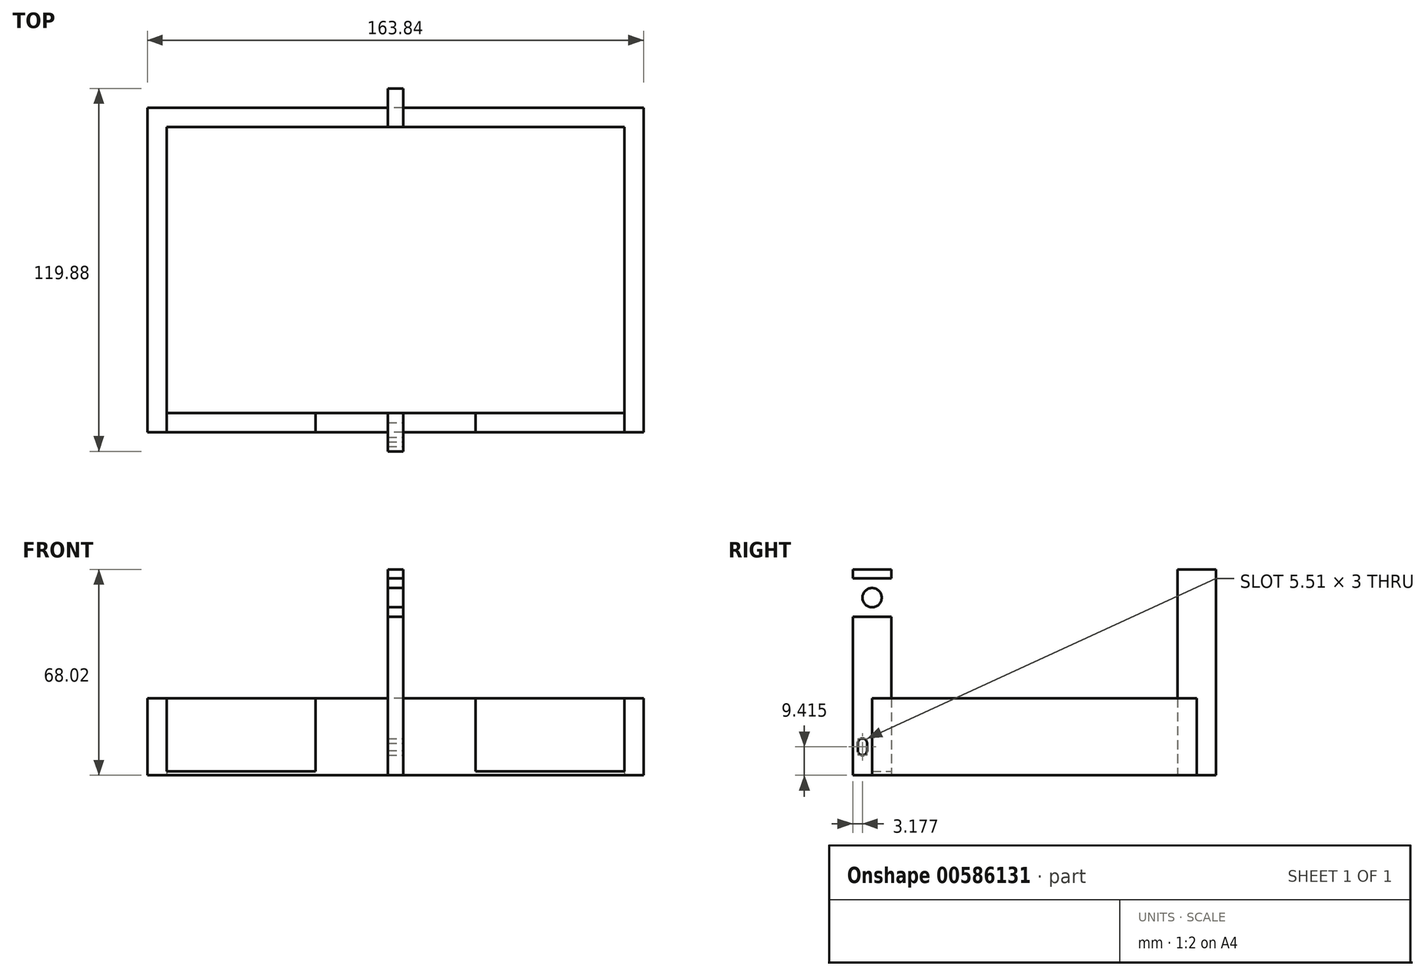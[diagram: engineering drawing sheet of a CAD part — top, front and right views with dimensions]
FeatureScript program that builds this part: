
annotation { "Feature Type Name" : "Feature", "Feature Type Description" : "" }
export const myFeature = defineFeature(function(context is Context, id is Id, definition is map)
    precondition{}
    {
        {
            var Q0;
            Q0=qCreatedBy(makeId("Top.planeOp"),FACE);
            var sketch = newSketch(context, id + "F0", { "sketchPlane" : qUnion([Q0])});
            skLineSegment(sketch, "E0.bottom", {"start": v(75.57, 47.24) * mm, "end": v(-75.57, 47.24) * mm});
            skLineSegment(sketch, "E0.top", {"start": v(75.57, -47.24) * mm, "end": v(-75.57, -47.24) * mm});
            skLineSegment(sketch, "E0.left", {"start": v(75.57, 47.24) * mm, "end": v(75.57, -47.24) * mm});
            skLineSegment(sketch, "E0.right", {"start": v(-75.57, 47.24) * mm, "end": v(-75.57, -47.24) * mm});
            skPoint(sketch, "E0.middle", {"position": v(0, 0) * mm});
            skLineSegment(sketch, "E1.bottom", {"start": v(81.92, 53.6) * mm, "end": v(-81.92, 53.6) * mm});
            skLineSegment(sketch, "E1.top", {"start": v(81.92, -53.6) * mm, "end": v(-81.92, -53.6) * mm});
            skLineSegment(sketch, "E1.left", {"start": v(81.92, 53.6) * mm, "end": v(81.92, -53.6) * mm});
            skLineSegment(sketch, "E1.right", {"start": v(-81.92, 53.6) * mm, "end": v(-81.92, -53.6) * mm});
            skLineSegment(sketch, "E2.bottom", {"start": v(-2.54, 47.24) * mm, "end": v(2.54, 47.24) * mm});
            skLineSegment(sketch, "E2.top", {"start": v(-2.54, 59.94) * mm, "end": v(2.54, 59.94) * mm});
            skLineSegment(sketch, "E2.left", {"start": v(-2.54, 47.24) * mm, "end": v(-2.54, 59.94) * mm});
            skLineSegment(sketch, "E2.right", {"start": v(2.54, 47.24) * mm, "end": v(2.54, 59.94) * mm});
            skPoint(sketch, "E2.middle", {"position": v(0, 53.6) * mm});
            skLineSegment(sketch, "E3.bottom", {"start": v(-2.54, -47.24) * mm, "end": v(2.54, -47.24) * mm});
            skLineSegment(sketch, "E3.top", {"start": v(-2.54, -59.94) * mm, "end": v(2.54, -59.94) * mm});
            skLineSegment(sketch, "E3.left", {"start": v(-2.54, -47.24) * mm, "end": v(-2.54, -59.94) * mm});
            skLineSegment(sketch, "E3.right", {"start": v(2.54, -47.24) * mm, "end": v(2.54, -59.94) * mm});
            skPoint(sketch, "E3.middle", {"position": v(0, -53.6) * mm});
            skLineSegment(sketch, "E4", {"start": v(-75.57, -47.24) * mm, "end": v(-75.57, -53.6) * mm});
            skLineSegment(sketch, "E5", {"start": v(75.57, -47.24) * mm, "end": v(75.57, -53.6) * mm});
            skLineSegment(sketch, "E6", {"start": v(-26.4, -47.24) * mm, "end": v(-26.4, -53.6) * mm});
            skLineSegment(sketch, "E7.MirrorCS", {"start": v(26.4, -47.24) * mm, "end": v(26.4, -53.6) * mm});
            skSolve(sketch);
        }
        {
            var Q0;
            {var subQ0=sQuery(id+"F0.wireOp",EDGE,"E4");Q0=makeQuery(id+"F0.imprint","IMPRINT",FACE,{"disambiguationData":[TD([[makeQuery(id+"F0.imprint","IMPRINT",EDGE,{"derivedFrom":subQ0}),1.0]])]});}
            var Q1;
            {var subQ6=sQuery(id+"F0.wireOp",EDGE,"E0.right");Q1=makeQuery(id+"F0.imprint","IMPRINT",FACE,{"disambiguationData":[TD([[makeQuery(id+"F0.imprint","IMPRINT",EDGE,{"derivedFrom":subQ6}),-1.0]])]});}
            var Q2;
            {var subQ5=sQuery(id+"F0.wireOp",EDGE,"E2.top");Q2=makeQuery(id+"F0.imprint","IMPRINT",FACE,{"disambiguationData":[TD([[makeQuery(id+"F0.imprint","IMPRINT",EDGE,{"derivedFrom":subQ5}),-1.0]])]});}
            var Q3;
            {var subQ5=sQuery(id+"F0.wireOp",EDGE,"E2.bottom");Q3=makeQuery(id+"F0.imprint","IMPRINT",FACE,{"disambiguationData":[TD([[makeQuery(id+"F0.imprint","IMPRINT",EDGE,{"derivedFrom":subQ5}),1.0]])]});}
            var Q4;
            {var subQ6=sQuery(id+"F0.wireOp",EDGE,"E0.left");Q4=makeQuery(id+"F0.imprint","IMPRINT",FACE,{"disambiguationData":[TD([[makeQuery(id+"F0.imprint","IMPRINT",EDGE,{"derivedFrom":subQ6}),1.0]])]});}
            var Q5;
            {var subQ0=sQuery(id+"F0.wireOp",EDGE,"E5");Q5=makeQuery(id+"F0.imprint","IMPRINT",FACE,{"disambiguationData":[TD([[makeQuery(id+"F0.imprint","IMPRINT",EDGE,{"derivedFrom":subQ0}),-1.0]])]});}
            var Q6;
            {var subQ3=sQuery(id+"F0.wireOp",EDGE,"E6");Q6=makeQuery(id+"F0.imprint","IMPRINT",FACE,{"disambiguationData":[TD([[makeQuery(id+"F0.imprint","IMPRINT",EDGE,{"derivedFrom":subQ3}),1.0]])]});}
            var Q7;
            {var subQ5=sQuery(id+"F0.wireOp",EDGE,"E3.bottom");Q7=makeQuery(id+"F0.imprint","IMPRINT",FACE,{"disambiguationData":[TD([[makeQuery(id+"F0.imprint","IMPRINT",EDGE,{"derivedFrom":subQ5}),-1.0]])]});}
            var Q8;
            {var subQ3=sQuery(id+"F0.wireOp",EDGE,"E7.MirrorCS");Q8=makeQuery(id+"F0.imprint","IMPRINT",FACE,{"disambiguationData":[TD([[makeQuery(id+"F0.imprint","IMPRINT",EDGE,{"derivedFrom":subQ3}),-1.0]])]});}
            var Q9;
            {var subQ5=sQuery(id+"F0.wireOp",EDGE,"E3.top");Q9=makeQuery(id+"F0.imprint","IMPRINT",FACE,{"disambiguationData":[TD([[makeQuery(id+"F0.imprint","IMPRINT",EDGE,{"derivedFrom":subQ5}),1.0]])]});}
            extrude(context, id + "F1", {"entities" : qUnion([Q0, Q1, Q2, Q3, Q4, Q5, Q6, Q7, Q8, Q9]), "depth" : 1.27 * mm, "offsetDistance" : 25.4 * mm});
        }
        {
            var Q0;
            {var subQ6=sQuery(id+"F0.wireOp",EDGE,"E0.right");Q0=makeQuery(id+"F0.imprint","IMPRINT",FACE,{"disambiguationData":[TD([[makeQuery(id+"F0.imprint","IMPRINT",EDGE,{"derivedFrom":subQ6}),-1.0]])]});}
            var Q1;
            {var subQ5=sQuery(id+"F0.wireOp",EDGE,"E2.top");Q1=makeQuery(id+"F0.imprint","IMPRINT",FACE,{"disambiguationData":[TD([[makeQuery(id+"F0.imprint","IMPRINT",EDGE,{"derivedFrom":subQ5}),-1.0]])]});}
            var Q2;
            {var subQ5=sQuery(id+"F0.wireOp",EDGE,"E2.bottom");Q2=makeQuery(id+"F0.imprint","IMPRINT",FACE,{"disambiguationData":[TD([[makeQuery(id+"F0.imprint","IMPRINT",EDGE,{"derivedFrom":subQ5}),1.0]])]});}
            var Q3;
            {var subQ6=sQuery(id+"F0.wireOp",EDGE,"E0.left");Q3=makeQuery(id+"F0.imprint","IMPRINT",FACE,{"disambiguationData":[TD([[makeQuery(id+"F0.imprint","IMPRINT",EDGE,{"derivedFrom":subQ6}),1.0]])]});}
            var Q4;
            {var subQ3=sQuery(id+"F0.wireOp",EDGE,"E7.MirrorCS");Q4=makeQuery(id+"F0.imprint","IMPRINT",FACE,{"disambiguationData":[TD([[makeQuery(id+"F0.imprint","IMPRINT",EDGE,{"derivedFrom":subQ3}),-1.0]])]});}
            var Q5;
            {var subQ5=sQuery(id+"F0.wireOp",EDGE,"E3.bottom");Q5=makeQuery(id+"F0.imprint","IMPRINT",FACE,{"disambiguationData":[TD([[makeQuery(id+"F0.imprint","IMPRINT",EDGE,{"derivedFrom":subQ5}),-1.0]])]});}
            var Q6;
            {var subQ3=sQuery(id+"F0.wireOp",EDGE,"E6");Q6=makeQuery(id+"F0.imprint","IMPRINT",FACE,{"disambiguationData":[TD([[makeQuery(id+"F0.imprint","IMPRINT",EDGE,{"derivedFrom":subQ3}),1.0]])]});}
            var Q7;
            {var subQ5=sQuery(id+"F0.wireOp",EDGE,"E3.top");Q7=makeQuery(id+"F0.imprint","IMPRINT",FACE,{"disambiguationData":[TD([[makeQuery(id+"F0.imprint","IMPRINT",EDGE,{"derivedFrom":subQ5}),1.0]])]});}
            extrude(context, id + "F2", {"entities" : qUnion([Q0, Q1, Q2, Q3, Q4, Q5, Q6, Q7]), "operationType" : NewBodyOperationType.ADD, "depth" : 25.4 * mm, "offsetDistance" : 25.4 * mm});
        }
        {
            var Q0;
            Q0=makeQuery(id+"F2.opExtrude","CAP_FACE",FACE,{"disambiguationData":[OSD([sQuery(id+"F0.wireOp",EDGE,"E0.bottom"),sQuery(id+"F0.wireOp",EDGE,"E0.left"),sQuery(id+"F0.wireOp",EDGE,"E0.right"),sQuery(id+"F0.wireOp",EDGE,"E1.bottom"),sQuery(id+"F0.wireOp",EDGE,"E1.top"),sQuery(id+"F0.wireOp",EDGE,"E1.left"),sQuery(id+"F0.wireOp",EDGE,"E1.right"),sQuery(id+"F0.wireOp",EDGE,"E2.bottom"),sQuery(id+"F0.wireOp",EDGE,"E2.top"),sQuery(id+"F0.wireOp",EDGE,"E2.left"),sQuery(id+"F0.wireOp",EDGE,"E2.right"),sQuery(id+"F0.wireOp",EDGE,"E4"),sQuery(id+"F0.wireOp",EDGE,"E5")])],"isStart":false});
            var sketch = newSketch(context, id + "F3", { "sketchPlane" : qUnion([Q0])});
            skLineSegment(sketch, "E8.bottom", {"start": v(-2.54, 59.94) * mm, "end": v(2.54, 59.94) * mm});
            skLineSegment(sketch, "E8.top", {"start": v(-2.54, 47.24) * mm, "end": v(2.54, 47.24) * mm});
            skLineSegment(sketch, "E8.left", {"start": v(-2.54, 59.94) * mm, "end": v(-2.54, 47.24) * mm});
            skLineSegment(sketch, "E8.right", {"start": v(2.54, 59.94) * mm, "end": v(2.54, 47.24) * mm});
            skLineSegment(sketch, "E9.MirrorCS", {"start": v(-2.54, -47.24) * mm, "end": v(2.54, -47.24) * mm});
            skLineSegment(sketch, "E10.MirrorCS", {"start": v(2.54, -59.94) * mm, "end": v(2.54, -47.24) * mm});
            skLineSegment(sketch, "E11.MirrorCS", {"start": v(-2.54, -59.94) * mm, "end": v(2.54, -59.94) * mm});
            skLineSegment(sketch, "E12.MirrorCS", {"start": v(-2.54, -59.94) * mm, "end": v(-2.54, -47.24) * mm});
            skSolve(sketch);
        }
        {
            var Q0;
            {var subQ5=sQuery(id+"F3.wireOp",EDGE,"E8.bottom");Q0=makeQuery(id+"F3.imprint","IMPRINT",FACE,{"disambiguationData":[TD([[makeQuery(id+"F3.imprint","IMPRINT",EDGE,{"derivedFrom":subQ5}),-1.0]])]});}
            var Q1;
            Q1=makeQuery(id+"F3.imprint","IMPRINT",FACE,{"disambiguationData":[TD([[makeQuery(id+"F3.imprint","IMPRINT",EDGE,{"derivedFrom":sQuery(id+"F3.wireOp",EDGE,"E9.MirrorCS")}),-1.0]])]});
            extrude(context, id + "F4", {"entities" : qUnion([Q0, Q1]), "operationType" : NewBodyOperationType.ADD, "depth" : 39.62 * mm + 3 * mm, "offsetDistance" : 25.4 * mm});
        }
        {
            var Q0;
            {var subQ0=sQuery(id+"F0.wireOp",EDGE,"E3.right");Q0=makeQuery(id+"F4.boolean.opBoolean","MERGE",FACE,{"derivedFrom":[makeQuery(id+"F2.boolean.opBoolean","MERGE",FACE,{"derivedFrom":[makeQuery(id+"F1.opExtrude","SWEPT_FACE",FACE,{"disambiguationData":[OSD([subQ0])]}),makeQuery(id+"F2.opExtrude","SWEPT_FACE",FACE,{"disambiguationData":[OSD([subQ0])]})]}),makeQuery(id+"F4.opExtrude","SWEPT_FACE",FACE,{"disambiguationData":[OSD([sQuery(id+"F3.wireOp",EDGE,"E10.MirrorCS")])]})]});}
            var sketch = newSketch(context, id + "F5", { "sketchPlane" : qUnion([Q0])});
            skCircle(sketch, "E13", {"center": v(-56.76, 8.16) * mm, "radius": 1.5 * mm});
            skCircle(sketch, "E14", {"center": v(-56.76, 10.67) * mm, "radius": 1.5 * mm});
            skLineSegment(sketch, "E15", {"start": v(-58.26, 10.63) * mm, "end": v(-58.26, 8.11) * mm});
            skLineSegment(sketch, "E16", {"start": v(-55.26, 10.67) * mm, "end": v(-55.26, 8.16) * mm});
            skSolve(sketch);
        }
        {
            var Q0;
            Q0 = qSketchRegion(id + "F5", true);
            var Q1;
            {var subQ0=sQuery(id+"F5.wireOp",EDGE,"E14");var subQ1=sQuery(id+"F5.wireOp",EDGE,"E13");var subQ2=makeQuery(id+"F5.imprint","INTERSECT",VERTEX,{"disambiguationData":[OD(0.0)],"derivedFrom":[subQ1,subQ0]});Q1=makeQuery(id+"F5.imprint","IMPRINT",FACE,{"disambiguationData":[TD([[makeQuery(id+"F5.imprint","IMPRINT",EDGE,{"disambiguationData":[TD([[subQ2,-1.0]])],"derivedFrom":subQ1}),1.0]])]});}
            extrude(context, id + "F6", {"entities" : qUnion([Q0, Q1]), "operationType" : NewBodyOperationType.REMOVE, "oppositeDirection" : true, "depth" : 25.4 * mm, "offsetDistance" : 25.4 * mm});
        }
        {
            var Q0;
            {var subQ0=sQuery(id+"F0.wireOp",EDGE,"E3.right");Q0=makeQuery(id+"F4.boolean.opBoolean","MERGE",FACE,{"derivedFrom":[makeQuery(id+"F2.boolean.opBoolean","MERGE",FACE,{"derivedFrom":[makeQuery(id+"F1.opExtrude","SWEPT_FACE",FACE,{"disambiguationData":[OSD([subQ0])]}),makeQuery(id+"F2.opExtrude","SWEPT_FACE",FACE,{"disambiguationData":[OSD([subQ0])]})]}),makeQuery(id+"F4.opExtrude","SWEPT_FACE",FACE,{"disambiguationData":[OSD([sQuery(id+"F3.wireOp",EDGE,"E10.MirrorCS")])]})]});}
            var sketch = newSketch(context, id + "F7", { "sketchPlane" : qUnion([Q0])});
            skLineSegment(sketch, "E17.bottom", {"start": v(-59.94, 68.02) * mm, "end": v(-47.24, 68.02) * mm});
            skLineSegment(sketch, "E17.top", {"start": v(-59.94, 65.02) * mm, "end": v(-47.24, 65.02) * mm});
            skLineSegment(sketch, "E17.left", {"start": v(-59.94, 68.02) * mm, "end": v(-59.94, 65.02) * mm});
            skLineSegment(sketch, "E17.right", {"start": v(-47.24, 68.02) * mm, "end": v(-47.24, 65.02) * mm});
            skLineSegment(sketch, "E18.bottom", {"start": v(-47.24, 65.02) * mm, "end": v(-59.94, 65.02) * mm});
            skLineSegment(sketch, "E18.top", {"start": v(-47.24, 52.32) * mm, "end": v(-59.94, 52.32) * mm});
            skLineSegment(sketch, "E18.left", {"start": v(-47.24, 65.02) * mm, "end": v(-47.24, 52.32) * mm});
            skLineSegment(sketch, "E18.right", {"start": v(-59.94, 65.02) * mm, "end": v(-59.94, 52.32) * mm});
            skLineSegment(sketch, "E19", {"start": v(-59.94, 65.02) * mm, "end": v(-47.24, 52.32) * mm});
            skCircle(sketch, "E20", {"center": v(-53.6, 58.67) * mm, "radius": 3.18 * mm});
            skCircle(sketch, "E21.MirrorC", {"center": v(53.6, 58.67) * mm, "radius": 3.18 * mm});
            skSolve(sketch);
        }
        {
            var Q0;
            Q0=makeQuery(id+"F7.imprint","IMPRINT",FACE,{"disambiguationData":[TD([[makeQuery(id+"F7.imprint","IMPRINT",EDGE,{"derivedFrom":sQuery(id+"F7.wireOp",EDGE,"E21.MirrorC")}),-1.0]])]});
            var Q1;
            {var subQ0=sQuery(id+"F7.wireOp",EDGE,"E20");var subQ1=sQuery(id+"F7.wireOp",EDGE,"E19");var subQ2=makeQuery(id+"F7.imprint","INTERSECT",VERTEX,{"disambiguationData":[OD(0.0)],"derivedFrom":[subQ1,subQ0]});Q1=makeQuery(id+"F7.imprint","IMPRINT",FACE,{"disambiguationData":[TD([[makeQuery(id+"F7.imprint","IMPRINT",EDGE,{"disambiguationData":[TD([[subQ2,-1.0]])],"derivedFrom":subQ1}),1.0]])]});}
            var Q2;
            {var subQ0=sQuery(id+"F7.wireOp",EDGE,"E20");var subQ1=sQuery(id+"F7.wireOp",EDGE,"E19");var subQ2=makeQuery(id+"F7.imprint","INTERSECT",VERTEX,{"disambiguationData":[OD(0.0)],"derivedFrom":[subQ1,subQ0]});Q2=makeQuery(id+"F7.imprint","IMPRINT",FACE,{"disambiguationData":[TD([[makeQuery(id+"F7.imprint","IMPRINT",EDGE,{"disambiguationData":[TD([[subQ2,-1.0]])],"derivedFrom":subQ1}),-1.0]])]});}
            extrude(context, id + "F8", {"entities" : qUnion([Q0, Q1, Q2]), "operationType" : NewBodyOperationType.REMOVE, "oppositeDirection" : true, "depth" : 25.4 * mm, "offsetDistance" : 25.4 * mm});
        }
    });
